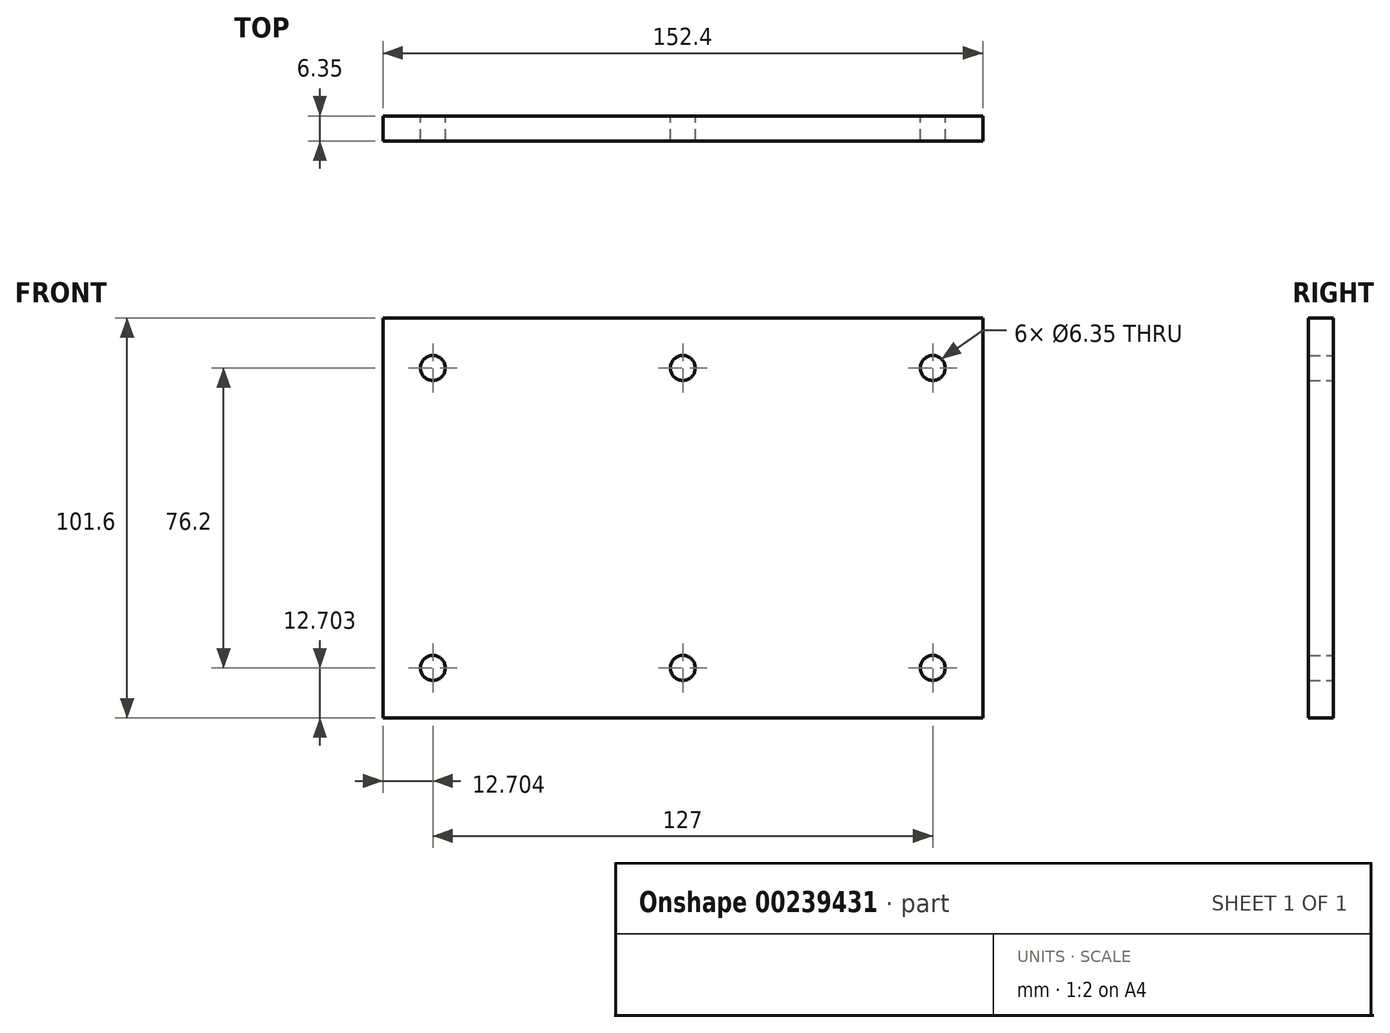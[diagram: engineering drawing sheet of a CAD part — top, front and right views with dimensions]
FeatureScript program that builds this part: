
annotation { "Feature Type Name" : "Feature", "Feature Type Description" : "" }
export const myFeature = defineFeature(function(context is Context, id is Id, definition is map)
    precondition{}
    {
        {
            var Q0;
            Q0=qCreatedBy(makeId("Front.planeOp"),FACE);
            var sketch = newSketch(context, id + "F0", { "sketchPlane" : qUnion([Q0])});
            skLineSegment(sketch, "E0.bottom", {"start": v(-63.17, 56.94) * mm, "end": v(89.23, 56.94) * mm});
            skLineSegment(sketch, "E0.top", {"start": v(-63.17, -44.66) * mm, "end": v(89.23, -44.66) * mm});
            skLineSegment(sketch, "E0.left", {"start": v(-63.17, 56.94) * mm, "end": v(-63.17, -44.66) * mm});
            skLineSegment(sketch, "E0.right", {"start": v(89.23, 56.94) * mm, "end": v(89.23, -44.66) * mm});
            skCircle(sketch, "E1", {"center": v(-50.47, 44.24) * mm, "radius": 3.18 * mm});
            skCircle(sketch, "E2", {"center": v(-50.47, -31.96) * mm, "radius": 3.18 * mm});
            skCircle(sketch, "E3", {"center": v(76.53, 44.24) * mm, "radius": 3.18 * mm});
            skCircle(sketch, "E4", {"center": v(76.53, -31.96) * mm, "radius": 3.18 * mm});
            skCircle(sketch, "E5", {"center": v(13.03, 44.24) * mm, "radius": 3.18 * mm});
            skCircle(sketch, "E6", {"center": v(13.03, -31.96) * mm, "radius": 3.18 * mm});
            skSolve(sketch);
        }
        {
            var Q0;
            Q0 = qSketchRegion(id + "F0", true);
            extrude(context, id + "F1", {"entities" : qUnion([Q0]), "depth" : 6.35 * mm});
        }
    });
